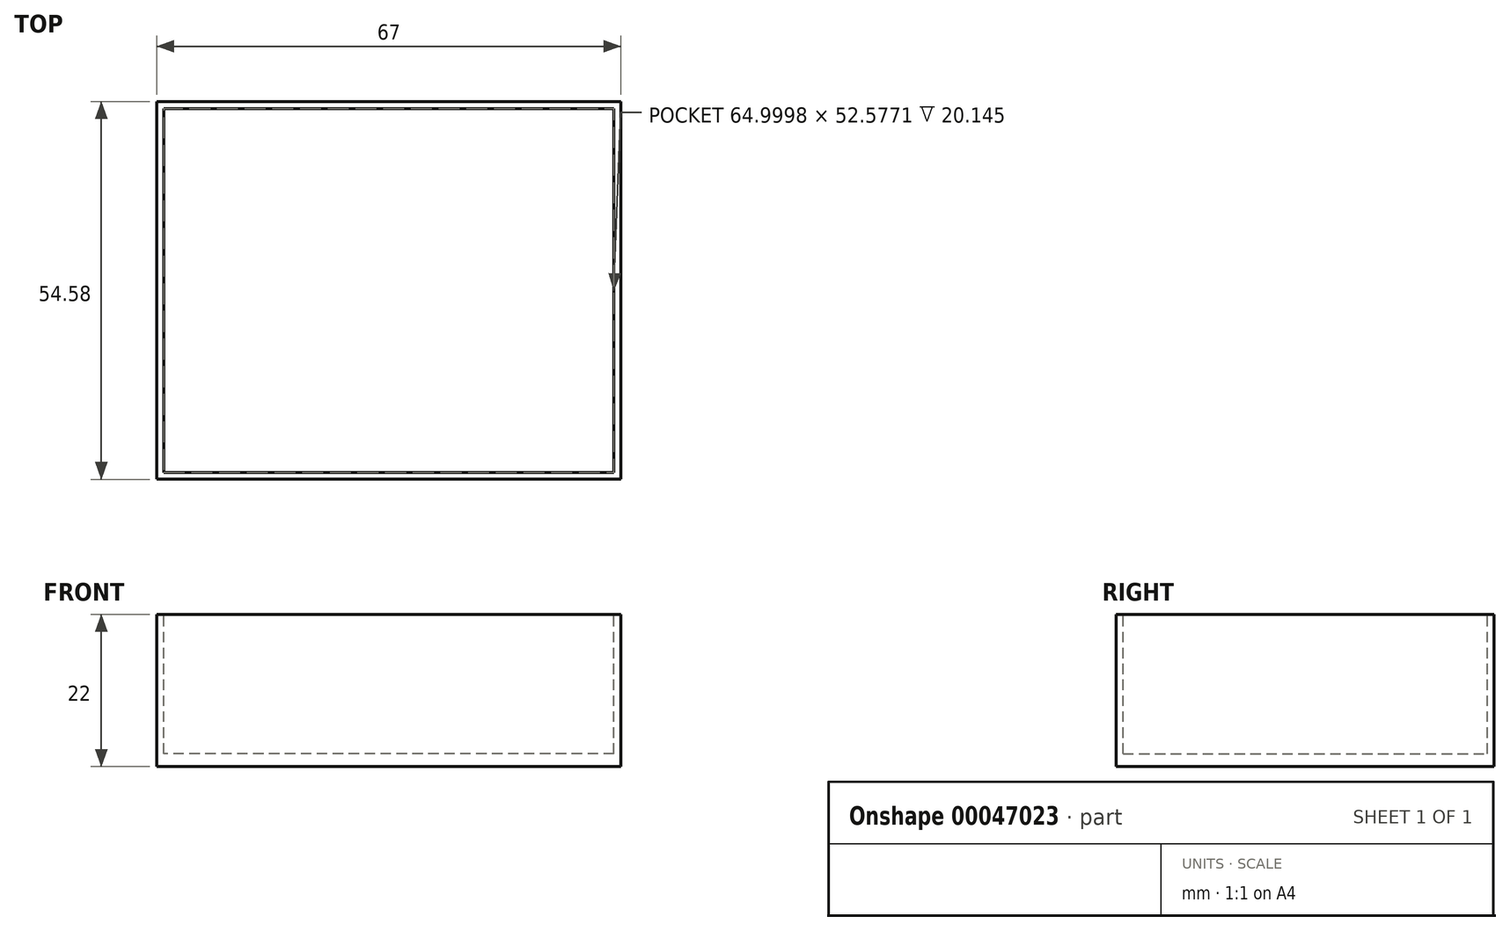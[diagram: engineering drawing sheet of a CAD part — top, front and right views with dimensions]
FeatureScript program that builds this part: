
annotation { "Feature Type Name" : "Feature", "Feature Type Description" : "" }
export const myFeature = defineFeature(function(context is Context, id is Id, definition is map)
    precondition{}
    {
        {
            var Q0;
            Q0=qCreatedBy(makeId("Top.planeOp"),FACE);
            var sketch = newSketch(context, id + "F0", { "sketchPlane" : qUnion([Q0])});
            skLineSegment(sketch, "E0.bottom", {"start": v(60.27, -26.87) * mm, "end": v(-60.5, -26.87) * mm});
            skLineSegment(sketch, "E0.top", {"start": v(60.27, 65.71) * mm, "end": v(-60.5, 65.71) * mm});
            skLineSegment(sketch, "E0.left", {"start": v(60.27, -26.87) * mm, "end": v(60.27, 65.71) * mm});
            skLineSegment(sketch, "E0.right", {"start": v(-60.5, -26.87) * mm, "end": v(-60.5, 65.71) * mm});
            skSolve(sketch);
        }
        {
            var Q0;
            Q0 = qSketchRegion(id + "F0", true);
            extrude(context, id + "F1", {"entities" : qUnion([Q0]), "depth" : 22 * mm});
        }
        {
            var Q0;
            Q0=makeQuery(id+"F1.opExtrude","SWEPT_FACE",FACE,{"disambiguationData":[OSD([sQuery(id+"F0.wireOp",EDGE,"E0.right")])]});
            extrude(context, id + "F2", {"entities" : qUnion([Q0]), "operationType" : NewBodyOperationType.REMOVE, "oppositeDirection" : true, "depth" : 53.78 * mm});
        }
        {
            var Q0;
            Q0=makeQuery(id+"F1.opExtrude","SWEPT_FACE",FACE,{"disambiguationData":[OSD([sQuery(id+"F0.wireOp",EDGE,"E0.top")])]});
            extrude(context, id + "F3", {"entities" : qUnion([Q0]), "operationType" : NewBodyOperationType.REMOVE, "oppositeDirection" : true, "depth" : 38 * mm});
        }
        {
            var Q0;
            Q0=makeQuery(id+"F1.opExtrude","CAP_FACE",FACE,{"disambiguationData":[OSD([sQuery(id+"F0.wireOp",EDGE,"E0.bottom"),sQuery(id+"F0.wireOp",EDGE,"E0.top"),sQuery(id+"F0.wireOp",EDGE,"E0.left"),sQuery(id+"F0.wireOp",EDGE,"E0.right")])],"isStart":false});
            var sketch = newSketch(context, id + "F4", { "sketchPlane" : qUnion([Q0])});
            skSolve(sketch);
        }
        {
            var Q0;
            Q0=makeQuery(id+"F4.imprint","IMPRINT",FACE,{"disambiguationData":[TD([[makeQuery(id+"F4.imprint","IMPRINT",EDGE,{"derivedFrom":makeQuery(id+"F1.opExtrude","CAP_EDGE",EDGE,{"disambiguationData":[OSD([sQuery(id+"F0.wireOp",EDGE,"E0.bottom")])],"isStart":false})}),-1.0]])]});
            var sketch = newSketch(context, id + "F5", { "sketchPlane" : qUnion([Q0])});
            skLineSegment(sketch, "E1.0", {"start": v(59.27, 26.71) * mm, "end": v(-5.73, 26.71) * mm});
            skLineSegment(sketch, "E1.1", {"start": v(59.27, -25.87) * mm, "end": v(59.27, 26.71) * mm});
            skLineSegment(sketch, "E1.2", {"start": v(59.27, -25.87) * mm, "end": v(-5.73, -25.87) * mm});
            skLineSegment(sketch, "E1.3", {"start": v(-5.73, -25.87) * mm, "end": v(-5.73, 26.71) * mm});
            skSolve(sketch);
        }
        {
            var Q0;
            Q0 = qSketchRegion(id + "F4", true);
            var Q1;
            Q1=makeQuery(id+"F5.imprint","IMPRINT",FACE,{"disambiguationData":[TD([[makeQuery(id+"F5.imprint","IMPRINT",EDGE,{"derivedFrom":sQuery(id+"F5.wireOp",EDGE,"E1.0")}),1.0]])]});
            extrude(context, id + "F6", {"entities" : qUnion([Q0, Q1]), "operationType" : NewBodyOperationType.REMOVE, "oppositeDirection" : true, "depth" : 20.15 * mm});
        }
    });
